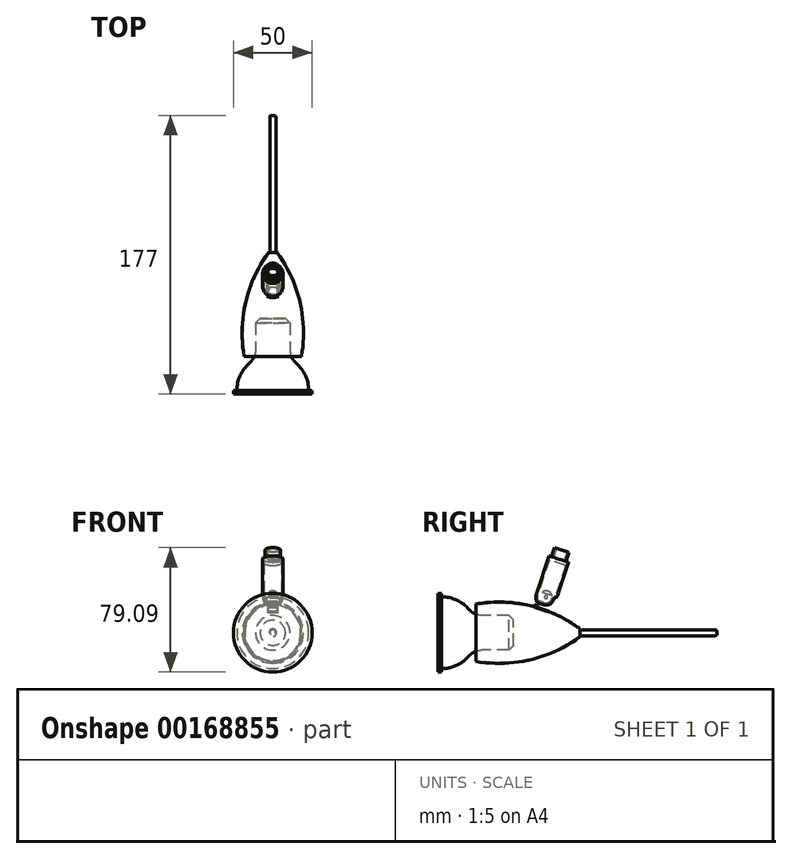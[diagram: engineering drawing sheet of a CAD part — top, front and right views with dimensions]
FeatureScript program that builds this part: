
annotation { "Feature Type Name" : "Feature", "Feature Type Description" : "" }
export const myFeature = defineFeature(function(context is Context, id is Id, definition is map)
    precondition{}
    {
        {
            var Q0;
            Q0=qCreatedBy(makeId("Right.planeOp"),FACE);
            var sketch = newSketch(context, id + "F0", { "sketchPlane" : qUnion([Q0])});
            skArc(sketch, "E0", {"start": v(66, 2.63) * mm, "mid": v(34.6, 17.17) * mm, "end": v(0, 18.25) * mm});
            skLineSegment(sketch, "E1", {"start": v(66, 2.63) * mm, "end": v(66, 0) * mm});
            skLineSegment(sketch, "E2", {"start": v(66, 0) * mm, "end": v(0, 0) * mm});
            skLineSegment(sketch, "E3", {"start": v(0, 0) * mm, "end": v(0, 18.25) * mm});
            skLineSegment(sketch, "E4", {"start": v(14.66, -67.05) * mm, "end": v(14.66, 19.5) * mm, "construction": true});
            skLineSegment(sketch, "E5", {"start": v(0, 0) * mm, "end": v(161.41, 0) * mm, "construction": true});
            skSolve(sketch);
        }
        {
            var Q0;
            Q0 = qSketchRegion(id + "F0", true);
            var Q1;
            Q1=sQuery(id+"F0.wireOp",EDGE,"E5");
            revolve(context, id + "F1", {"entities" : qUnion([Q0]), "axis" : qUnion([Q1]), "revolveType" : RevolveType.FULL});
        }
        {
            var Q0;
            Q0=makeQuery(id+"F1.opRevolve","SWEPT_FACE",FACE,{"disambiguationData":[OSD([sQuery(id+"F0.wireOp",EDGE,"E3")])]});
            shell(context, id + "F2", {"entities" : qUnion([Q0]), "thickness" : 0.5 * mm});
        }
        {
            var Q0;
            Q0=makeQuery(id+"F1.opRevolve","SWEPT_FACE",FACE,{"disambiguationData":[OSD([sQuery(id+"F0.wireOp",EDGE,"E1")])]});
            var sketch = newSketch(context, id + "F3", { "sketchPlane" : qUnion([Q0])});
            skCircle(sketch, "E6", {"center": v(0, 0) * mm, "radius": 1.9 * mm});
            skSolve(sketch);
        }
        {
            var Q0;
            Q0 = qSketchRegion(id + "F3", true);
            extrude(context, id + "F4", {"entities" : qUnion([Q0]), "operationType" : NewBodyOperationType.ADD, "depth" : 87 * mm});
        }
        {
            var Q0;
            Q0=makeQuery(id+"F4.opExtrude","CAP_EDGE",EDGE,{"disambiguationData":[OSD([sQuery(id+"F3.wireOp",EDGE,"E6")])],"isStart":false});
            fillet(context, id + "F5", {"entities" : qUnion([Q0]), "radius" : 1 * mm, "tangentPropagation" : true, "allowEdgeOverflow" : false});
        }
        {
            var Q0;
            Q0=qCreatedBy(makeId("Right.planeOp"),FACE);
            var sketch = newSketch(context, id + "F6", { "sketchPlane" : qUnion([Q0])});
            skPoint(sketch, "E7", {"position": v(42, 15.07) * mm});
            skLineSegment(sketch, "E8", {"start": v(42, 15.07) * mm, "end": v(46.42, 28.34) * mm, "construction": true});
            skLineSegment(sketch, "E9", {"start": v(35.96, 17.08) * mm, "end": v(48.04, 13.06) * mm, "construction": true});
            skLineSegment(sketch, "E10", {"start": v(36.94, 15.7) * mm, "end": v(37.65, 17.83) * mm});
            skLineSegment(sketch, "E11", {"start": v(37.65, 17.83) * mm, "end": v(38.6, 17.52) * mm});
            skLineSegment(sketch, "E12", {"start": v(38.6, 17.52) * mm, "end": v(40.73, 23.92) * mm});
            skLineSegment(sketch, "E13.MirrorCS", {"start": v(46.43, 12.54) * mm, "end": v(47.14, 14.67) * mm});
            skLineSegment(sketch, "E14.MirrorCS", {"start": v(46.2, 14.99) * mm, "end": v(48.32, 21.4) * mm});
            skLineSegment(sketch, "E15.MirrorCS", {"start": v(47.14, 14.67) * mm, "end": v(46.2, 14.99) * mm});
            skArc(sketch, "E16", {"start": v(48.32, 21.4) * mm, "mid": v(45.8, 26.45) * mm, "end": v(40.73, 23.92) * mm});
            skCircle(sketch, "E17", {"center": v(44.53, 22.66) * mm, "radius": 1 * mm});
            skLineSegment(sketch, "E18", {"start": v(36.94, 15.7) * mm, "end": v(46.43, 12.54) * mm});
            skSolve(sketch);
        }
        {
            var Q0;
            Q0 = qSketchRegion(id + "F6", true);
            extrude(context, id + "F7", {"entities" : qUnion([Q0]), "operationType" : NewBodyOperationType.ADD, "endBound" : BoundingType.SYMMETRIC, "depth" : 5.9 * mm});
        }
        {
            var Q0;
            Q0=makeQuery(id+"F7.opExtrude","CAP_EDGE",EDGE,{"disambiguationData":[OSD([sQuery(id+"F6.wireOp",EDGE,"E14.MirrorCS")])],"isStart":false});
            var Q1;
            Q1=makeQuery(id+"F7.opExtrude","CAP_EDGE",EDGE,{"disambiguationData":[OSD([sQuery(id+"F6.wireOp",EDGE,"E14.MirrorCS")])],"isStart":true});
            var Q2;
            Q2=makeQuery(id+"F7.opExtrude","CAP_EDGE",EDGE,{"disambiguationData":[OSD([sQuery(id+"F6.wireOp",EDGE,"E12")])],"isStart":false});
            var Q3;
            Q3=makeQuery(id+"F7.opExtrude","CAP_EDGE",EDGE,{"disambiguationData":[OSD([sQuery(id+"F6.wireOp",EDGE,"E12")])],"isStart":true});
            fillet(context, id + "F8", {"entities" : qUnion([Q0, Q1, Q2, Q3]), "radius" : 2.95 * mm, "tangentPropagation" : true, "allowEdgeOverflow" : false});
        }
        {
            var Q0;
            {var subQ1=sQuery(id+"F6.wireOp",EDGE,"E13.MirrorCS");Q0=makeQuery(id+"F7.boolean.opBoolean","SPLIT",EDGE,{"disambiguationData":[TD([makeQuery(id+"F1.opRevolve","SWEPT_FACE",FACE,{"disambiguationData":[OSD([sQuery(id+"F0.wireOp",EDGE,"E0")])]})])],"derivedFrom":makeQuery(id+"F7.opExtrude","CAP_EDGE",EDGE,{"disambiguationData":[OSD([subQ1])],"isStart":false})});}
            var Q1;
            {var subQ1=sQuery(id+"F6.wireOp",EDGE,"E13.MirrorCS");Q1=makeQuery(id+"F7.boolean.opBoolean","SPLIT",EDGE,{"disambiguationData":[TD([makeQuery(id+"F1.opRevolve","SWEPT_FACE",FACE,{"disambiguationData":[OSD([sQuery(id+"F0.wireOp",EDGE,"E0")])]})])],"derivedFrom":makeQuery(id+"F7.opExtrude","CAP_EDGE",EDGE,{"disambiguationData":[OSD([subQ1])],"isStart":true})});}
            var Q2;
            {var subQ0=sQuery(id+"F6.wireOp",EDGE,"E10");Q2=makeQuery(id+"F7.boolean.opBoolean","SPLIT",EDGE,{"disambiguationData":[TD([makeQuery(id+"F1.opRevolve","SWEPT_FACE",FACE,{"disambiguationData":[OSD([sQuery(id+"F0.wireOp",EDGE,"E0")])]})])],"derivedFrom":makeQuery(id+"F7.opExtrude","CAP_EDGE",EDGE,{"disambiguationData":[OSD([subQ0])],"isStart":false})});}
            var Q3;
            {var subQ0=sQuery(id+"F6.wireOp",EDGE,"E10");Q3=makeQuery(id+"F7.boolean.opBoolean","SPLIT",EDGE,{"disambiguationData":[TD([makeQuery(id+"F1.opRevolve","SWEPT_FACE",FACE,{"disambiguationData":[OSD([sQuery(id+"F0.wireOp",EDGE,"E0")])]})])],"derivedFrom":makeQuery(id+"F7.opExtrude","CAP_EDGE",EDGE,{"disambiguationData":[OSD([subQ0])],"isStart":true})});}
            fillet(context, id + "F9", {"entities" : qUnion([Q0, Q1, Q2, Q3]), "radius" : 2 * mm, "tangentPropagation" : true, "allowEdgeOverflow" : false});
        }
        {
            var Q0;
            Q0=makeQuery(id+"F1.opRevolve","SWEPT_EDGE",EDGE,{"disambiguationData":[OSD([sQuery(id+"F0.wireOp",EDGE,"E0"),sQuery(id+"F0.wireOp",EDGE,"E1")])]});
            fillet(context, id + "F10", {"entities" : qUnion([Q0]), "radius" : 0.3 * mm, "tangentPropagation" : true, "allowEdgeOverflow" : false});
        }
        {
            var Q0;
            Q0=sQuery(id+"F6.wireOp",EDGE,"E8");
            cPlane(context, id + "F11", {"entities" : qUnion([Q0]), "cplaneType" : CPlaneType.LINE_ANGLE, "offset" : 25 * mm, "angle" : 90 * degree, "width" : 150 * mm, "height" : 150 * mm});
        }
        {
            var Q0;
            Q0=qCreatedBy(makeId("Right.planeOp"),FACE);
            var sketch = newSketch(context, id + "F12", { "sketchPlane" : qUnion([Q0])});
            skLineSegment(sketch, "E19", {"start": v(46.42, 48.9) * mm, "end": v(38.36, 24.71) * mm});
            skArc(sketch, "E20", {"start": v(38.36, 24.71) * mm, "mid": v(38.71, 19.75) * mm, "end": v(42.47, 16.5) * mm});
            skLineSegment(sketch, "E21", {"start": v(46.58, 46.22) * mm, "end": v(39.3, 24.4) * mm});
            skArc(sketch, "E22", {"start": v(39.3, 24.4) * mm, "mid": v(39.6, 20.2) * mm, "end": v(42.79, 17.44) * mm});
            skLineSegment(sketch, "E23", {"start": v(42.47, 16.5) * mm, "end": v(42.79, 17.44) * mm});
            skLineSegment(sketch, "E24", {"start": v(46.58, 46.22) * mm, "end": v(51.8, 44.48) * mm});
            skLineSegment(sketch, "E25", {"start": v(51.8, 44.48) * mm, "end": v(52.58, 46.85) * mm});
            skLineSegment(sketch, "E26", {"start": v(46.42, 48.9) * mm, "end": v(52.58, 46.85) * mm});
            skSolve(sketch);
        }
        {
            var Q0;
            Q0 = qSketchRegion(id + "F12", true);
            var Q1;
            Q1=sQuery(id+"F6.wireOp",EDGE,"E8");
            revolve(context, id + "F13", {"entities" : qUnion([Q0]), "axis" : qUnion([Q1]), "revolveType" : RevolveType.FULL});
        }
        {
            var Q0;
            Q0=sQuery(id+"F6.wireOp",EDGE,"E9");
            cPlane(context, id + "F14", {"entities" : qUnion([Q0]), "cplaneType" : CPlaneType.LINE_ANGLE, "offset" : 25 * mm, "angle" : 0 * degree, "width" : 150 * mm, "height" : 150 * mm});
        }
        {
            var Q0;
            Q0=qCreatedBy(id+"F14.planeOp",FACE);
            var sketch = newSketch(context, id + "F15", { "sketchPlane" : qUnion([Q0])});
            skArc(sketch, "E27", {"start": v(-4, 35.09) * mm, "mid": v(0, 31.09) * mm, "end": v(4, 35.09) * mm});
            skLineSegment(sketch, "E28", {"start": v(4, 35.09) * mm, "end": v(4, 45.09) * mm});
            skLineSegment(sketch, "E29", {"start": v(-4, 35.09) * mm, "end": v(-4, 45.09) * mm});
            skLineSegment(sketch, "E30", {"start": v(4, 45.09) * mm, "end": v(-4, 45.09) * mm});
            skSolve(sketch);
        }
        {
            var Q0;
            Q0 = qSketchRegion(id + "F15", true);
            extrude(context, id + "F16", {"entities" : qUnion([Q0]), "operationType" : NewBodyOperationType.REMOVE, "depth" : 10 * mm});
        }
        {
            var Q0;
            Q0=makeQuery(id+"F16.boolean.opBoolean","COPY",EDGE,{"derivedFrom":makeQuery(id+"F16.opExtrude","CAP_EDGE",EDGE,{"disambiguationData":[OSD([sQuery(id+"F15.wireOp",EDGE,"E29")])],"isStart":false})});
            var Q1;
            Q1=makeQuery(id+"F16.boolean.opBoolean","COPY",EDGE,{"derivedFrom":makeQuery(id+"F16.opExtrude","CAP_EDGE",EDGE,{"disambiguationData":[OSD([sQuery(id+"F15.wireOp",EDGE,"E28")])],"isStart":false})});
            fillet(context, id + "F17", {"entities" : qUnion([Q0, Q1]), "radius" : 2 * mm, "tangentPropagation" : true, "allowEdgeOverflow" : false});
        }
        {
            var Q0;
            Q0=qCreatedBy(makeId("Right.planeOp"),FACE);
            var sketch = newSketch(context, id + "F18", { "sketchPlane" : qUnion([Q0])});
            skCircle(sketch, "E31", {"center": v(44.53, 22.66) * mm, "radius": 1 * mm});
            skSolve(sketch);
        }
        {
            var Q0;
            Q0 = qSketchRegion(id + "F18", true);
            extrude(context, id + "F19", {"entities" : qUnion([Q0]), "operationType" : NewBodyOperationType.ADD, "endBound" : BoundingType.UP_TO_NEXT, "depth" : 25 * mm, "hasSecondDirection" : true, "secondDirectionBound" : SecondDirectionBoundingType.UP_TO_NEXT, "secondDirectionOppositeDirection" : true, "secondDirectionDepth" : 25 * mm});
        }
        {
            var Q0;
            Q0=makeQuery(id+"F13.opRevolve","SWEPT_FACE",FACE,{"disambiguationData":[OSD([sQuery(id+"F12.wireOp",EDGE,"E26")])]});
            var sketch = newSketch(context, id + "F20", { "sketchPlane" : qUnion([Q0])});
            skCircle(sketch, "E32", {"center": v(0, 35.09) * mm, "radius": 4.9 * mm});
            skCircle(sketch, "E33", {"center": v(0, 35.09) * mm, "radius": 3.5 * mm});
            skSolve(sketch);
        }
        {
            var Q0;
            Q0 = qSketchRegion(id + "F20", true);
            extrude(context, id + "F21", {"entities" : qUnion([Q0]), "operationType" : NewBodyOperationType.ADD, "depth" : 6 * mm});
        }
        {
            var Q0;
            Q0=qCreatedBy(makeId("Front.planeOp"),FACE);
            cPlane(context, id + "F22", {"entities" : qUnion([Q0]), "cplaneType" : CPlaneType.OFFSET, "offset" : 24 * mm, "oppositeDirection" : true, "width" : 150 * mm, "height" : 150 * mm});
        }
        {
            var Q0;
            Q0=qCreatedBy(makeId("Right.planeOp"),FACE);
            var sketch = newSketch(context, id + "F23", { "sketchPlane" : qUnion([Q0])});
            skLineSegment(sketch, "E34", {"start": v(0, 0) * mm, "end": v(24, 0) * mm, "construction": true});
            skLineSegment(sketch, "E35", {"start": v(24, 0) * mm, "end": v(24, 11) * mm});
            skLineSegment(sketch, "E36", {"start": v(24, 11) * mm, "end": v(4, 11) * mm});
            skLineSegment(sketch, "E37", {"start": v(-24, 0) * mm, "end": v(-24, 25) * mm});
            skLineSegment(sketch, "E38", {"start": v(-24, 25) * mm, "end": v(-21.7, 25) * mm});
            skLineSegment(sketch, "E39", {"start": v(-21.7, 25) * mm, "end": v(-21.7, 22.8) * mm});
            skLineSegment(sketch, "E40", {"start": v(-24, 0) * mm, "end": v(24, 0) * mm});
            skArc(sketch, "E41", {"start": v(-4.4, 14.86) * mm, "mid": v(-12.19, 20.72) * mm, "end": v(-21.7, 22.8) * mm});
            skArc(sketch, "E42", {"start": v(-4.4, 14.86) * mm, "mid": v(-0.63, 12.01) * mm, "end": v(4, 11) * mm});
            skSolve(sketch);
        }
        {
            var Q0;
            Q0 = qSketchRegion(id + "F23", true);
            var Q1;
            Q1=sQuery(id+"F23.wireOp",EDGE,"E34");
            revolve(context, id + "F24", {"entities" : qUnion([Q0]), "axis" : qUnion([Q1]), "revolveType" : RevolveType.FULL});
        }
        {
            var Q0;
            Q0=makeQuery(id+"F24.opRevolve","SWEPT_EDGE",EDGE,{"disambiguationData":[OSD([sQuery(id+"F23.wireOp",EDGE,"E35"),sQuery(id+"F23.wireOp",EDGE,"E36")])]});
            chamfer(context, id + "F25", {"entities" : qUnion([Q0]), "width" : 3 * mm, "tangentPropagation" : true});
        }
    });
